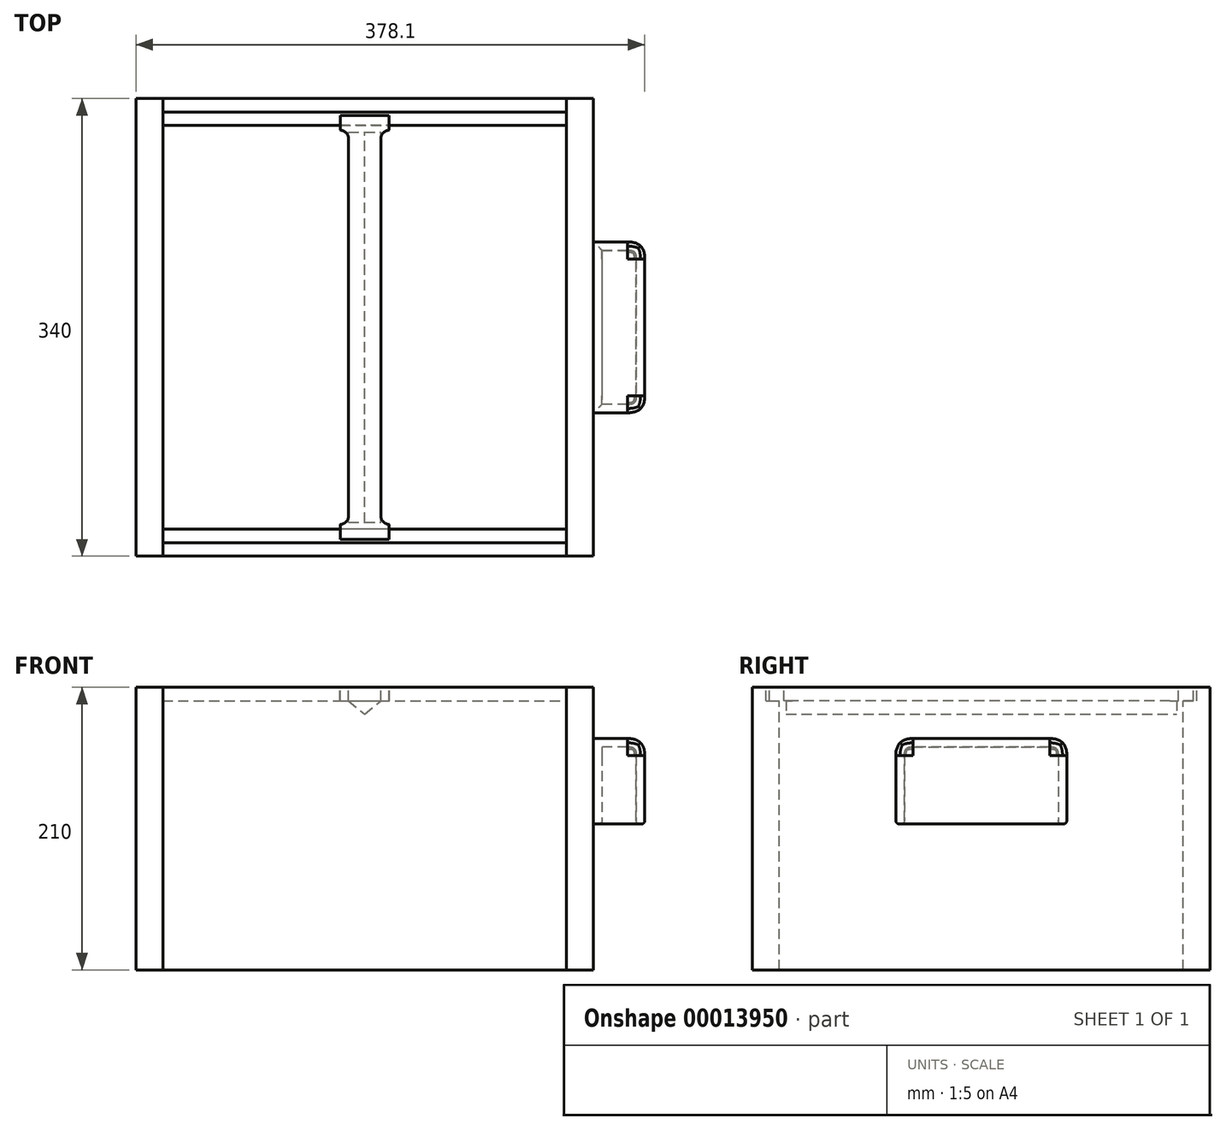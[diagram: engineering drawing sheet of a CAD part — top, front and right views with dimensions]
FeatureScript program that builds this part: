
annotation { "Feature Type Name" : "Feature", "Feature Type Description" : "" }
export const myFeature = defineFeature(function(context is Context, id is Id, definition is map)
    precondition{}
    {
        {
            var Q0;
            Q0=qCreatedBy(makeId("Top.planeOp"),FACE);
            var sketch = newSketch(context, id + "F0", { "sketchPlane" : qUnion([Q0])});
            skLineSegment(sketch, "E0.bottom", {"start": v(150, 150) * mm, "end": v(-150, 150) * mm});
            skLineSegment(sketch, "E0.top", {"start": v(150, -150) * mm, "end": v(-150, -150) * mm});
            skLineSegment(sketch, "E0.left", {"start": v(150, 150) * mm, "end": v(150, -150) * mm});
            skLineSegment(sketch, "E0.right", {"start": v(-150, 150) * mm, "end": v(-150, -150) * mm});
            skPoint(sketch, "E0.middle", {"position": v(0, 0) * mm});
            skLineSegment(sketch, "E1", {"start": v(-150, 150) * mm, "end": v(-150, 170) * mm});
            skLineSegment(sketch, "E2", {"start": v(-150, 170) * mm, "end": v(150, 170) * mm});
            skLineSegment(sketch, "E3", {"start": v(150, 170) * mm, "end": v(150, 150) * mm});
            skLineSegment(sketch, "E4", {"start": v(-150, -150) * mm, "end": v(-150, -170) * mm});
            skLineSegment(sketch, "E5", {"start": v(-150, -170) * mm, "end": v(150, -170) * mm});
            skLineSegment(sketch, "E6", {"start": v(150, -170) * mm, "end": v(150, -150) * mm});
            skLineSegment(sketch, "E7", {"start": v(-150, -170) * mm, "end": v(-170, -170) * mm});
            skLineSegment(sketch, "E8", {"start": v(-170, -170) * mm, "end": v(-170, 170) * mm});
            skLineSegment(sketch, "E9", {"start": v(-170, 170) * mm, "end": v(-150, 170) * mm});
            skLineSegment(sketch, "E10", {"start": v(150, 170) * mm, "end": v(170, 170) * mm});
            skLineSegment(sketch, "E11", {"start": v(170, 170) * mm, "end": v(170, -170) * mm});
            skLineSegment(sketch, "E12", {"start": v(170, -170) * mm, "end": v(150, -170) * mm});
            skSolve(sketch);
        }
        {
            var Q0;
            Q0=makeQuery(id+"F0.imprint","IMPRINT",FACE,{"disambiguationData":[TD([[makeQuery(id+"F0.imprint","IMPRINT",EDGE,{"derivedFrom":sQuery(id+"F0.wireOp",EDGE,"E0.right")}),-1.0]])]});
            extrude(context, id + "F1", {"entities" : qUnion([Q0]), "oppositeDirection" : true, "depth" : 210 * mm});
        }
        {
            var Q0;
            Q0=makeQuery(id+"F0.imprint","IMPRINT",FACE,{"disambiguationData":[TD([[makeQuery(id+"F0.imprint","IMPRINT",EDGE,{"derivedFrom":sQuery(id+"F0.wireOp",EDGE,"E0.top")}),1.0]])]});
            extrude(context, id + "F2", {"entities" : qUnion([Q0]), "oppositeDirection" : true, "depth" : 210 * mm});
        }
        {
            var Q0;
            Q0=makeQuery(id+"F0.imprint","IMPRINT",FACE,{"disambiguationData":[TD([[makeQuery(id+"F0.imprint","IMPRINT",EDGE,{"derivedFrom":sQuery(id+"F0.wireOp",EDGE,"E0.left")}),1.0]])]});
            extrude(context, id + "F3", {"entities" : qUnion([Q0]), "oppositeDirection" : true, "depth" : 210 * mm});
        }
        {
            var Q0;
            Q0=makeQuery(id+"F0.imprint","IMPRINT",FACE,{"disambiguationData":[TD([[makeQuery(id+"F0.imprint","IMPRINT",EDGE,{"derivedFrom":sQuery(id+"F0.wireOp",EDGE,"E0.bottom")}),-1.0]])]});
            extrude(context, id + "F4", {"entities" : qUnion([Q0]), "oppositeDirection" : true, "depth" : 210 * mm});
        }
        {
            var Q0;
            Q0=makeQuery(id+"F0.imprint","IMPRINT",FACE,{"disambiguationData":[TD([[makeQuery(id+"F0.imprint","IMPRINT",EDGE,{"derivedFrom":sQuery(id+"F0.wireOp",EDGE,"E0.top")}),1.0]])]});
            var sketch = newSketch(context, id + "F5", { "sketchPlane" : qUnion([Q0])});
            skPoint(sketch, "E13.0", {"position": v(-150, -150) * mm});
            skPoint(sketch, "E14.0", {"position": v(150, -160) * mm});
            skLineSegment(sketch, "E15.bottom", {"start": v(-150, -150) * mm, "end": v(150, -150) * mm});
            skLineSegment(sketch, "E15.top", {"start": v(-150, -160) * mm, "end": v(150, -160) * mm});
            skLineSegment(sketch, "E15.left", {"start": v(-150, -150) * mm, "end": v(-150, -160) * mm});
            skLineSegment(sketch, "E15.right", {"start": v(150, -150) * mm, "end": v(150, -160) * mm});
            skPoint(sketch, "E16.0", {"position": v(-150, 150) * mm});
            skPoint(sketch, "E17.0", {"position": v(150, 160) * mm});
            skLineSegment(sketch, "E18.bottom", {"start": v(-150, 150) * mm, "end": v(150, 150) * mm});
            skLineSegment(sketch, "E18.top", {"start": v(-150, 160) * mm, "end": v(150, 160) * mm});
            skLineSegment(sketch, "E18.left", {"start": v(-150, 150) * mm, "end": v(-150, 160) * mm});
            skLineSegment(sketch, "E18.right", {"start": v(150, 150) * mm, "end": v(150, 160) * mm});
            skSolve(sketch);
        }
        {
            var Q0;
            Q0 = qSketchRegion(id + "F5", true);
            extrude(context, id + "F6", {"entities" : qUnion([Q0]), "operationType" : NewBodyOperationType.REMOVE, "oppositeDirection" : true, "depth" : 10 * mm});
        }
        {
            var Q0;
            Q0=makeQuery(id+"F0.imprint","IMPRINT",FACE,{"disambiguationData":[TD([[makeQuery(id+"F0.imprint","IMPRINT",EDGE,{"derivedFrom":sQuery(id+"F0.wireOp",EDGE,"E0.bottom")}),1.0]])]});
            var sketch = newSketch(context, id + "F7", { "sketchPlane" : qUnion([Q0])});
            skLineSegment(sketch, "E19.bottom", {"start": v(12, 157.5) * mm, "end": v(-12, 157.5) * mm});
            skLineSegment(sketch, "E19.top", {"start": v(12, -157.5) * mm, "end": v(-12, -157.5) * mm});
            skLineSegment(sketch, "E19.left", {"start": v(12, 140.13) * mm, "end": v(12, -140.13) * mm});
            skLineSegment(sketch, "E19.right", {"start": v(-12, 140.13) * mm, "end": v(-12, -140.13) * mm});
            skPoint(sketch, "E19.middle", {"position": v(0, 0) * mm});
            skLineSegment(sketch, "E20", {"start": v(-12, 157.5) * mm, "end": v(-18, 157.5) * mm});
            skLineSegment(sketch, "E21", {"start": v(-18, 157.5) * mm, "end": v(-18, 146.48) * mm});
            skLineSegment(sketch, "E22", {"start": v(-18.35, 146.48) * mm, "end": v(-18, 146.48) * mm});
            skPoint(sketch, "E23.visualSharp", {"position": v(-12, 146.48) * mm});
            skArc(sketch, "E23.filletArc", {"start": v(-12, 140.13) * mm, "mid": v(-13.86, 144.62) * mm, "end": v(-18.35, 146.48) * mm});
            skLineSegment(sketch, "E24", {"start": v(0, 170.49) * mm, "end": v(0, -182.7) * mm, "construction": true});
            skPoint(sketch, "E24.endSnap0", {"position": v(0, -157.5) * mm});
            skArc(sketch, "E25.MirrorCS", {"start": v(12, 140.13) * mm, "mid": v(13.86, 144.62) * mm, "end": v(18.35, 146.48) * mm});
            skLineSegment(sketch, "E26.MirrorCS", {"start": v(18.35, 146.48) * mm, "end": v(18, 146.48) * mm});
            skLineSegment(sketch, "E27.MirrorCS", {"start": v(18, 157.5) * mm, "end": v(18, 146.48) * mm});
            skLineSegment(sketch, "E28.MirrorCS", {"start": v(12, 157.5) * mm, "end": v(18, 157.5) * mm});
            skLineSegment(sketch, "E29", {"start": v(-233.4, 0) * mm, "end": v(237.18, 0) * mm, "construction": true});
            skArc(sketch, "E30.MirrorCS", {"start": v(12, -140.13) * mm, "mid": v(13.86, -144.62) * mm, "end": v(18.35, -146.48) * mm});
            skLineSegment(sketch, "E31.MirrorCS", {"start": v(18.35, -146.48) * mm, "end": v(18, -146.48) * mm});
            skLineSegment(sketch, "E32.MirrorCS", {"start": v(18, -157.5) * mm, "end": v(18, -146.48) * mm});
            skLineSegment(sketch, "E33.MirrorCS", {"start": v(12, -157.5) * mm, "end": v(18, -157.5) * mm});
            skLineSegment(sketch, "E34.MirrorCS", {"start": v(-12, -157.5) * mm, "end": v(-18, -157.5) * mm});
            skLineSegment(sketch, "E35.MirrorCS", {"start": v(-18, -157.5) * mm, "end": v(-18, -146.48) * mm});
            skLineSegment(sketch, "E36.MirrorCS", {"start": v(-18.35, -146.48) * mm, "end": v(-18, -146.48) * mm});
            skArc(sketch, "E37.MirrorCS", {"start": v(-12, -140.13) * mm, "mid": v(-13.86, -144.62) * mm, "end": v(-18.35, -146.48) * mm});
            skSolve(sketch);
        }
        {
            var Q0;
            Q0=makeQuery(id+"F7.imprint","IMPRINT",FACE,{"disambiguationData":[TD([[makeQuery(id+"F7.imprint","IMPRINT",EDGE,{"derivedFrom":sQuery(id+"F7.wireOp",EDGE,"E19.left")}),-1.0]])]});
            var Q1;
            Q1=makeQuery(id+"F7.imprint","IMPRINT",FACE,{"disambiguationData":[TD([[makeQuery(id+"F7.imprint","IMPRINT",EDGE,{"derivedFrom":sQuery(id+"F7.wireOp",EDGE,"E19.bottom")}),1.0]])]});
            var Q2;
            Q2=makeQuery(id+"F7.imprint","IMPRINT",FACE,{"disambiguationData":[TD([[makeQuery(id+"F7.imprint","IMPRINT",EDGE,{"derivedFrom":sQuery(id+"F7.wireOp",EDGE,"E19.top")}),-1.0]])]});
            extrude(context, id + "F8", {"entities" : qUnion([Q0, Q1, Q2]), "oppositeDirection" : true, "depth" : 10 * mm});
        }
        {
            var Q0;
            Q0=qCreatedBy(makeId("Front.planeOp"),FACE);
            var sketch = newSketch(context, id + "F9", { "sketchPlane" : qUnion([Q0])});
            skLineSegment(sketch, "E38", {"start": v(0, -20) * mm, "end": v(0, 0) * mm, "construction": true});
            skPoint(sketch, "E39.0", {"position": v(12, -10) * mm});
            skPoint(sketch, "E40.0", {"position": v(-12, -10) * mm});
            skLineSegment(sketch, "E41", {"start": v(0, -20) * mm, "end": v(12, -10) * mm});
            skLineSegment(sketch, "E42", {"start": v(-12, -10) * mm, "end": v(0, -20) * mm});
            skLineSegment(sketch, "E43", {"start": v(-12, -10) * mm, "end": v(12, -10) * mm});
            skSolve(sketch);
        }
        {
            var Q0;
            Q0=makeQuery(id+"F9.imprint","IMPRINT",FACE,{"disambiguationData":[TD([[makeQuery(id+"F9.imprint","IMPRINT",EDGE,{"derivedFrom":sQuery(id+"F9.wireOp",EDGE,"E41")}),1.0]])]});
            extrude(context, id + "F10", {"entities" : qUnion([Q0]), "operationType" : NewBodyOperationType.ADD, "endBound" : BoundingType.SYMMETRIC, "depth" : 290 * mm});
        }
        {
            var Q0;
            Q0=makeQuery(id+"F3.opExtrude","SWEPT_FACE",FACE,{"disambiguationData":[OSD([sQuery(id+"F0.wireOp",EDGE,"E11")])]});
            var sketch = newSketch(context, id + "F11", { "sketchPlane" : qUnion([Q0])});
            skLineSegment(sketch, "E44.bottom", {"start": v(63.5, -38.1) * mm, "end": v(-63.5, -38.1) * mm});
            skLineSegment(sketch, "E44.top", {"start": v(63.5, -101.6) * mm, "end": v(-63.5, -101.6) * mm});
            skLineSegment(sketch, "E44.left", {"start": v(63.5, -38.1) * mm, "end": v(63.5, -101.6) * mm});
            skLineSegment(sketch, "E44.right", {"start": v(-63.5, -38.1) * mm, "end": v(-63.5, -101.6) * mm});
            skPoint(sketch, "E44.middle", {"position": v(0, -69.85) * mm});
            skPoint(sketch, "E44.middle.positionSnap0", {"position": v(0, 0) * mm});
            skPoint(sketch, "E44.centerSnap0", {"position": v(0, 0) * mm});
            skSolve(sketch);
        }
        {
            var Q0;
            Q0 = qSketchRegion(id + "F11", true);
            extrude(context, id + "F12", {"entities" : qUnion([Q0]), "depth" : 38.1 * mm});
        }
        {
            var Q0;
            Q0=makeQuery(id+"F12.opExtrude","CAP_EDGE",EDGE,{"disambiguationData":[OSD([sQuery(id+"F11.wireOp",EDGE,"E44.right")])],"isStart":false});
            var Q1;
            Q1=makeQuery(id+"F12.opExtrude","SWEPT_EDGE",EDGE,{"disambiguationData":[OSD([sQuery(id+"F11.wireOp",EDGE,"E44.bottom"),sQuery(id+"F11.wireOp",EDGE,"E44.right")])]});
            var Q2;
            Q2=makeQuery(id+"F12.opExtrude","CAP_EDGE",EDGE,{"disambiguationData":[OSD([sQuery(id+"F11.wireOp",EDGE,"E44.bottom")])],"isStart":false});
            var Q3;
            Q3=makeQuery(id+"F12.opExtrude","SWEPT_EDGE",EDGE,{"disambiguationData":[OSD([sQuery(id+"F11.wireOp",EDGE,"E44.bottom"),sQuery(id+"F11.wireOp",EDGE,"E44.left")])]});
            var Q4;
            Q4=makeQuery(id+"F12.opExtrude","CAP_EDGE",EDGE,{"disambiguationData":[OSD([sQuery(id+"F11.wireOp",EDGE,"E44.left")])],"isStart":false});
            fillet(context, id + "F13", {"entities" : qUnion([Q0, Q1, Q2, Q3, Q4]), "radius" : 12.7 * mm, "tangentPropagation" : true, "rho" : 0.5, "crossSection" : FilletCrossSection.CONIC, "allowEdgeOverflow" : false});
        }
        {
            var Q0;
            Q0=makeQuery(id+"F12.opExtrude","SWEPT_FACE",FACE,{"disambiguationData":[OSD([sQuery(id+"F11.wireOp",EDGE,"E44.top")])]});
            shell(context, id + "F14", {"entities" : qUnion([Q0]), "thickness" : 6.35 * mm});
        }
        {
            var Q0;
            {var subQ0=sQuery(id+"F11.wireOp",EDGE,"E44.top");Q0=makeQuery(id+"F14.opShell","OFFSET_EDGE",EDGE,{"disambiguationData":[OSD([subQ0]),TDD([makeQuery(id+"F12.opExtrude","CAP_EDGE",EDGE,{"disambiguationData":[OSD([subQ0])],"isStart":true})])]});}
            var Q1;
            {var subQ0=sQuery(id+"F11.wireOp",EDGE,"E44.right");var subQ1=sQuery(id+"F11.wireOp",EDGE,"E44.top");Q1=makeQuery(id+"F14.opShell","OFFSET_EDGE",EDGE,{"disambiguationData":[OSD([subQ1,subQ0]),TDD([makeQuery(id+"F12.opExtrude","SWEPT_EDGE",EDGE,{"disambiguationData":[OSD([subQ1,subQ0])]})])]});}
            var Q2;
            {var subQ0=sQuery(id+"F11.wireOp",EDGE,"E44.top");var subQ1=sQuery(id+"F11.wireOp",EDGE,"E44.right");Q2=makeQuery(id+"F14.opShell","OFFSET_EDGE",EDGE,{"disambiguationData":[OSD([subQ0,subQ1]),TDD([makeQuery(id+"F13.opFillet","BLEND_EDGE",EDGE,{"blendedFrom":[makeQuery(id+"F12.opExtrude","CAP_EDGE",EDGE,{"disambiguationData":[OSD([subQ1])],"isStart":false}),makeQuery(id+"F12.opExtrude","SWEPT_FACE",FACE,{"disambiguationData":[OSD([subQ0])]})],"blendedInto":[makeQuery(id+"F12.opExtrude","SWEPT_FACE",FACE,{"disambiguationData":[OSD([subQ0])]})]})])]});}
            var Q3;
            {var subQ0=sQuery(id+"F11.wireOp",EDGE,"E44.top");Q3=makeQuery(id+"F14.opShell","OFFSET_EDGE",EDGE,{"disambiguationData":[OSD([subQ0]),TDD([makeQuery(id+"F12.opExtrude","CAP_EDGE",EDGE,{"disambiguationData":[OSD([subQ0])],"isStart":false})])]});}
            var Q4;
            Q4=makeQuery(id+"F12.opExtrude","CAP_EDGE",EDGE,{"disambiguationData":[OSD([sQuery(id+"F11.wireOp",EDGE,"E44.top")])],"isStart":false});
            var Q5;
            Q5=makeQuery(id+"F13.opFillet","BLEND_EDGE",EDGE,{"blendedFrom":[makeQuery(id+"F12.opExtrude","CAP_EDGE",EDGE,{"disambiguationData":[OSD([sQuery(id+"F11.wireOp",EDGE,"E44.right")])],"isStart":false}),makeQuery(id+"F12.opExtrude","SWEPT_FACE",FACE,{"disambiguationData":[OSD([sQuery(id+"F11.wireOp",EDGE,"E44.top")])]})],"blendedInto":[makeQuery(id+"F12.opExtrude","SWEPT_FACE",FACE,{"disambiguationData":[OSD([sQuery(id+"F11.wireOp",EDGE,"E44.top")])]})]});
            fillet(context, id + "F15", {"entities" : qUnion([Q0, Q1, Q2, Q3, Q4, Q5]), "radius" : 2.54 * mm, "tangentPropagation" : true, "allowEdgeOverflow" : false});
        }
    });
